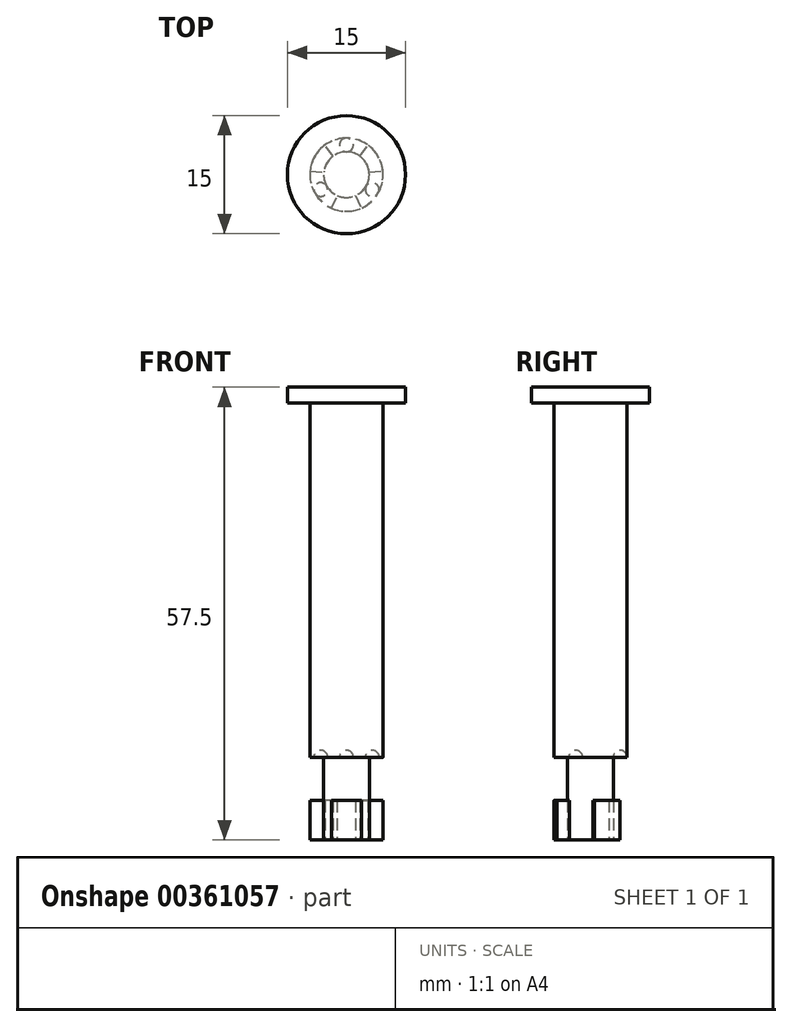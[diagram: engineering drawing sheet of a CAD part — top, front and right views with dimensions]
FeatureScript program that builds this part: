
annotation { "Feature Type Name" : "Feature", "Feature Type Description" : "" }
export const myFeature = defineFeature(function(context is Context, id is Id, definition is map)
    precondition{}
    {
        {
            var Q0;
            Q0=qCreatedBy(makeId("Top.planeOp"),FACE);
            var sketch = newSketch(context, id + "F0", { "sketchPlane" : qUnion([Q0])});
            skArc(sketch, "E0", {"start": v(-2.73, 3.76) * mm, "mid": v(-4.03, 2.32) * mm, "end": v(-4.62, 0.49) * mm});
            skCircle(sketch, "E1.0", {"center": v(0, 0) * mm, "radius": 2.9 * mm});
            skLineSegment(sketch, "E2", {"start": v(1.7, 2.35) * mm, "end": v(2.73, 3.76) * mm});
            skLineSegment(sketch, "E3", {"start": v(-1.7, 2.35) * mm, "end": v(-2.73, 3.76) * mm});
            skLineSegment(sketch, "E4.1.1", {"start": v(-1.18, -2.65) * mm, "end": v(-1.9, -4.25) * mm, "construction": true});
            skLineSegment(sketch, "E4.1.2", {"start": v(-2.88, 0.3) * mm, "end": v(-4.62, 0.49) * mm, "construction": true});
            skArc(sketch, "E4.2.0", {"start": v(-2.73, 3.76) * mm, "mid": v(-4.03, 2.33) * mm, "end": v(-4.62, 0.49) * mm});
            skLineSegment(sketch, "E4.2.1", {"start": v(2.88, 0.3) * mm, "end": v(4.62, 0.49) * mm, "construction": true});
            skLineSegment(sketch, "E4.2.2", {"start": v(1.18, -2.65) * mm, "end": v(1.9, -4.25) * mm, "construction": true});
            skLineSegment(sketch, "E5", {"start": v(-1.9, -4.25) * mm, "end": v(-1.18, -2.65) * mm});
            skLineSegment(sketch, "E6", {"start": v(-4.62, 0.49) * mm, "end": v(-2.88, 0.3) * mm});
            skLineSegment(sketch, "E7", {"start": v(1.18, -2.65) * mm, "end": v(1.9, -4.25) * mm});
            skLineSegment(sketch, "E8", {"start": v(2.88, 0.3) * mm, "end": v(4.62, 0.49) * mm});
            skArc(sketch, "E9.trimOffspring", {"start": v(-1.9, -4.25) * mm, "mid": v(0, -4.65) * mm, "end": v(1.9, -4.25) * mm});
            skArc(sketch, "E10.trimOffspring", {"start": v(4.62, 0.49) * mm, "mid": v(4.03, 2.33) * mm, "end": v(2.73, 3.76) * mm});
            skArc(sketch, "E11.trimOffspring", {"start": v(4.62, 0.49) * mm, "mid": v(4.03, 2.32) * mm, "end": v(2.73, 3.76) * mm});
            skSolve(sketch);
        }
        {
            var Q0;
            {var subQ0=sQuery(id+"F0.wireOp",EDGE,"E3");Q0=makeQuery(id+"F0.imprint","IMPRINT",FACE,{"disambiguationData":[TD([[makeQuery(id+"F0.imprint","IMPRINT",EDGE,{"derivedFrom":subQ0}),1.0]])]});}
            var Q1;
            {var subQ0=sQuery(id+"F0.wireOp",EDGE,"E2");Q1=makeQuery(id+"F0.imprint","IMPRINT",FACE,{"disambiguationData":[TD([[makeQuery(id+"F0.imprint","IMPRINT",EDGE,{"derivedFrom":subQ0}),-1.0]])]});}
            var Q2;
            {var subQ0=sQuery(id+"F0.wireOp",EDGE,"E5");Q2=makeQuery(id+"F0.imprint","IMPRINT",FACE,{"disambiguationData":[TD([[makeQuery(id+"F0.imprint","IMPRINT",EDGE,{"derivedFrom":subQ0}),-1.0]])]});}
            extrude(context, id + "F1", {"entities" : qUnion([Q0, Q1, Q2]), "offsetDistance" : 25 * mm, "depth" : 5 * mm});
        }
        {
            var Q0;
            {var subQ0=sQuery(id+"F0.wireOp",EDGE,"E1.0");var subQ4=makeQuery(id+"F0.imprint","INTERSECT",VERTEX,{"derivedFrom":[subQ0,sQuery(id+"F0.wireOp",EDGE,"E2")]});Q0=makeQuery(id+"F0.imprint","IMPRINT",FACE,{"disambiguationData":[TD([[makeQuery(id+"F0.imprint","IMPRINT",EDGE,{"disambiguationData":[TD([[subQ4,1.0]])],"derivedFrom":subQ0}),1.0]])]});}
            extrude(context, id + "F2", {"entities" : qUnion([Q0]), "offsetDistance" : 25 * mm, "depth" : (5 + 5.5) * mm});
        }
        {
            var Q0;
            Q0=makeQuery(id+"F2.opExtrude","CAP_FACE",FACE,{"disambiguationData":[OSD([sQuery(id+"F0.wireOp",EDGE,"E1.0")])],"isStart":false});
            var sketch = newSketch(context, id + "F3", { "sketchPlane" : qUnion([Q0])});
            skCircle(sketch, "E12", {"center": v(0, 0) * mm, "radius": 4.65 * mm});
            skSolve(sketch);
        }
        {
            var Q0;
            Q0=makeQuery(id+"F3.imprint","IMPRINT",FACE,{"disambiguationData":[TD([[makeQuery(id+"F3.imprint","IMPRINT",EDGE,{"derivedFrom":sQuery(id+"F3.wireOp",EDGE,"E12")}),1.0]])]});
            var Q1;
            Q1=makeQuery(id+"F3.imprint","IMPRINT",FACE,{"disambiguationData":[TD([[makeQuery(id+"F3.imprint","IMPRINT",EDGE,{"derivedFrom":makeQuery(id+"F2.opExtrude","CAP_EDGE",EDGE,{"disambiguationData":[OSD([sQuery(id+"F0.wireOp",EDGE,"E1.0")])],"isStart":false})}),1.0]])]});
            extrude(context, id + "F4", {"entities" : qUnion([Q0, Q1]), "operationType" : NewBodyOperationType.ADD, "offsetDistance" : 25 * mm, "depth" : 45 * mm});
        }
        {
            var Q0;
            Q0=makeQuery(id+"F4.opExtrude","CAP_FACE",FACE,{"disambiguationData":[OSD([sQuery(id+"F3.wireOp",EDGE,"E12")])],"isStart":false});
            var sketch = newSketch(context, id + "F5", { "sketchPlane" : qUnion([Q0])});
            skCircle(sketch, "E13", {"center": v(0, 0) * mm, "radius": 7.5 * mm});
            skSolve(sketch);
        }
        {
            var Q0;
            Q0=makeQuery(id+"F5.imprint","IMPRINT",FACE,{"disambiguationData":[TD([[makeQuery(id+"F5.imprint","IMPRINT",EDGE,{"derivedFrom":sQuery(id+"F5.wireOp",EDGE,"E13")}),1.0]])]});
            var Q1;
            Q1=makeQuery(id+"F5.imprint","IMPRINT",FACE,{"disambiguationData":[TD([[makeQuery(id+"F5.imprint","IMPRINT",EDGE,{"derivedFrom":makeQuery(id+"F4.opExtrude","CAP_EDGE",EDGE,{"disambiguationData":[OSD([sQuery(id+"F3.wireOp",EDGE,"E12")])],"isStart":false})}),1.0]])]});
            extrude(context, id + "F6", {"entities" : qUnion([Q0, Q1]), "operationType" : NewBodyOperationType.ADD, "depth" : 2 * mm, "offsetDistance" : 25 * mm});
        }
        {
            var Q0;
            Q0=makeQuery(id+"F4.opExtrude","CAP_FACE",FACE,{"disambiguationData":[OSD([sQuery(id+"F3.wireOp",EDGE,"E12")])],"isStart":true});
            var sketch = newSketch(context, id + "F7", { "sketchPlane" : qUnion([Q0])});
            skLineSegment(sketch, "E14", {"start": v(0, 0) * mm, "end": v(0, -4.65) * mm, "construction": true});
            skLineSegment(sketch, "E15", {"start": v(-2.51, 1.45) * mm, "end": v(-4.03, 2.32) * mm, "construction": true});
            skLineSegment(sketch, "E16", {"start": v(2.51, 1.45) * mm, "end": v(4.03, 2.33) * mm, "construction": true});
            skCircle(sketch, "E17", {"center": v(0, 0) * mm, "radius": 3.78 * mm, "construction": true});
            skPoint(sketch, "E18", {"position": v(-3.27, 1.89) * mm});
            skPoint(sketch, "E19", {"position": v(0, -3.78) * mm});
            skPoint(sketch, "E20", {"position": v(3.27, 1.89) * mm});
            skArc(sketch, "E21", {"start": v(-4.03, 2.32) * mm, "mid": v(-3.7, 1.13) * mm, "end": v(-2.51, 1.45) * mm});
            skArc(sketch, "E22", {"start": v(4.03, 2.33) * mm, "mid": v(2.83, 2.65) * mm, "end": v(2.51, 1.45) * mm});
            skPoint(sketch, "E23", {"position": v(0, -2.9) * mm});
            skArc(sketch, "E24", {"start": v(0, -4.65) * mm, "mid": v(0.88, -3.78) * mm, "end": v(0, -2.9) * mm});
            skLineSegment(sketch, "E25", {"start": v(-4.03, 2.32) * mm, "end": v(-2.51, 1.45) * mm});
            skLineSegment(sketch, "E26", {"start": v(2.51, 1.45) * mm, "end": v(4.03, 2.33) * mm});
            skLineSegment(sketch, "E27", {"start": v(0, -2.9) * mm, "end": v(0, -4.65) * mm});
            skSolve(sketch);
        }
        {
            var Q0;
            Q0=makeQuery(id+"F7.imprint","IMPRINT",FACE,{"disambiguationData":[TD([[makeQuery(id+"F7.imprint","IMPRINT",EDGE,{"derivedFrom":sQuery(id+"F7.wireOp",EDGE,"E21")}),1.0]])]});
            var Q1;
            Q1=sQuery(id+"F7.wireOp",EDGE,"E25");
            revolve(context, id + "F8", {"operationType" : NewBodyOperationType.REMOVE, "entities" : qUnion([Q0]), "axis" : qUnion([Q1]), "revolveType" : RevolveType.FULL});
        }
        {
            var Q0;
            Q0=makeQuery(id+"F7.imprint","IMPRINT",FACE,{"disambiguationData":[TD([[makeQuery(id+"F7.imprint","IMPRINT",EDGE,{"derivedFrom":sQuery(id+"F7.wireOp",EDGE,"E22")}),1.0]])]});
            var Q1;
            Q1=sQuery(id+"F7.wireOp",EDGE,"E26");
            revolve(context, id + "F9", {"operationType" : NewBodyOperationType.REMOVE, "entities" : qUnion([Q0]), "axis" : qUnion([Q1]), "revolveType" : RevolveType.FULL, "oppositeDirection" : true});
        }
        {
            var Q0;
            Q0=makeQuery(id+"F7.imprint","IMPRINT",FACE,{"disambiguationData":[TD([[makeQuery(id+"F7.imprint","IMPRINT",EDGE,{"derivedFrom":sQuery(id+"F7.wireOp",EDGE,"E24")}),1.0]])]});
            var Q1;
            Q1=sQuery(id+"F7.wireOp",EDGE,"E27");
            revolve(context, id + "F10", {"operationType" : NewBodyOperationType.REMOVE, "entities" : qUnion([Q0]), "axis" : qUnion([Q1]), "revolveType" : RevolveType.FULL, "oppositeDirection" : true});
        }
    });
